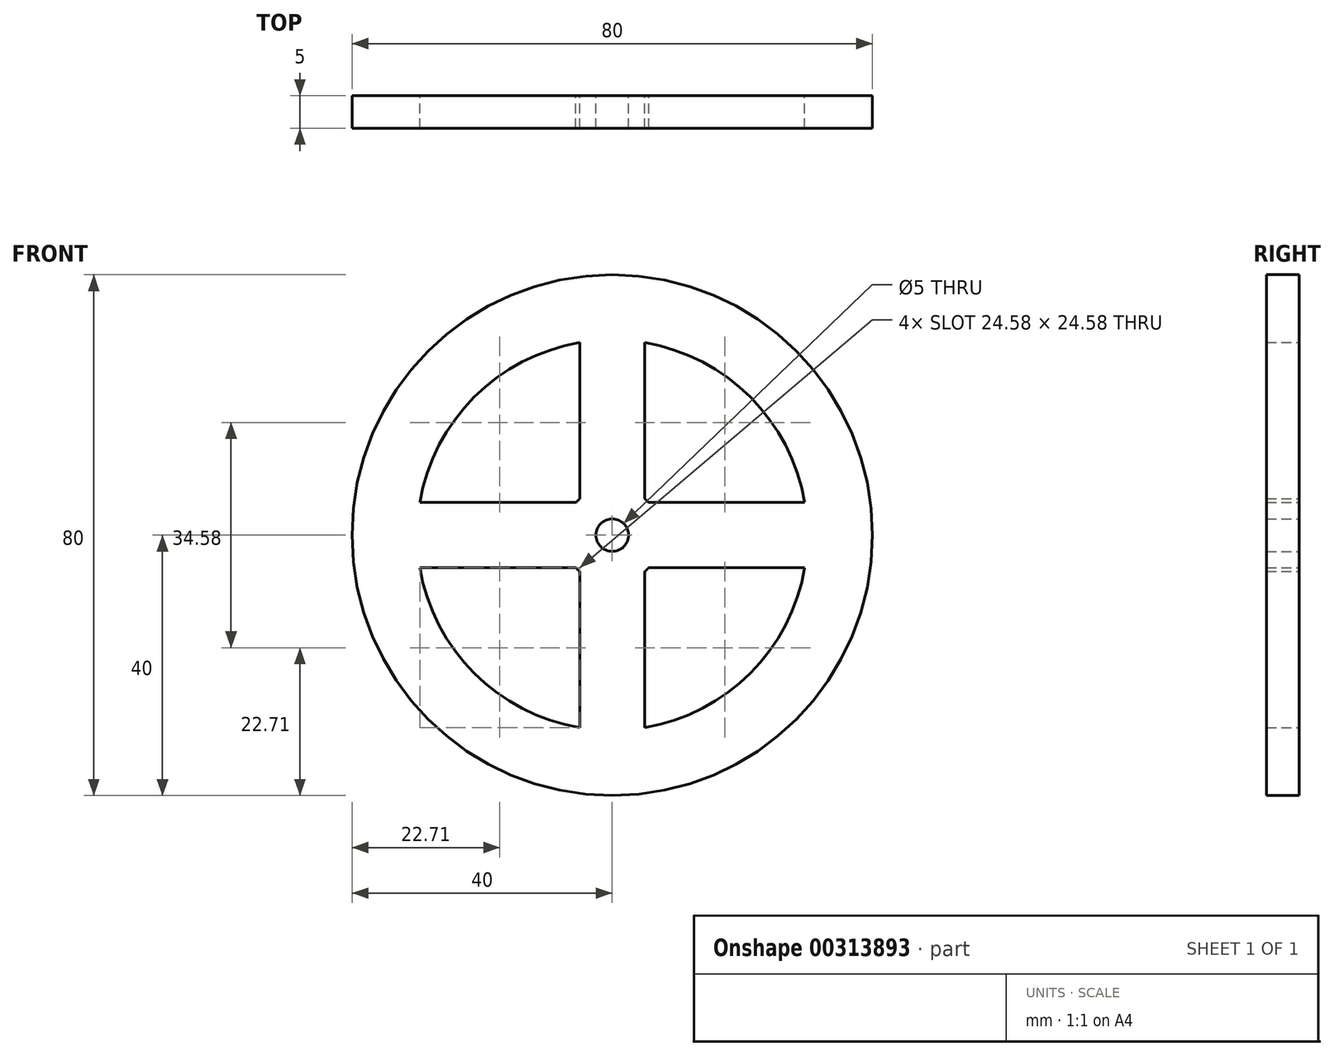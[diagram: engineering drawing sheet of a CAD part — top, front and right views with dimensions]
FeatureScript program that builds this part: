
annotation { "Feature Type Name" : "Feature", "Feature Type Description" : "" }
export const myFeature = defineFeature(function(context is Context, id is Id, definition is map)
    precondition{}
    {
        {
            var Q0;
            Q0=qCreatedBy(makeId("Front.planeOp"),FACE);
            var sketch = newSketch(context, id + "F0", { "sketchPlane" : qUnion([Q0])});
            skCircle(sketch, "E0", {"center": v(0, 0) * mm, "radius": 40 * mm});
            skArc(sketch, "E1", {"start": v(29.58, 5) * mm, "mid": v(21.21, 21.21) * mm, "end": v(5, 29.58) * mm});
            skArc(sketch, "E2", {"start": v(-5.6, -5) * mm, "mid": v(-5.3, -5.3) * mm, "end": v(-5, -5.6) * mm});
            skCircle(sketch, "E3", {"center": v(0, 0) * mm, "radius": 2.5 * mm});
            skLineSegment(sketch, "E4", {"start": v(0, 7.5) * mm, "end": v(0, 30) * mm, "construction": true});
            skLineSegment(sketch, "E5", {"start": v(0, -2.5) * mm, "end": v(0, -30) * mm});
            skLineSegment(sketch, "E6", {"start": v(-7.5, 0) * mm, "end": v(-30, 0) * mm, "construction": true});
            skLineSegment(sketch, "E7", {"start": v(0, 0) * mm, "end": v(0, 2.5) * mm, "construction": true});
            skLineSegment(sketch, "E8", {"start": v(0, 0) * mm, "end": v(2.5, 0) * mm, "construction": true});
            skLineSegment(sketch, "E9", {"start": v(0, 0) * mm, "end": v(0, -30) * mm, "construction": true});
            skLineSegment(sketch, "E10", {"start": v(0, 0) * mm, "end": v(-2.5, 0) * mm, "construction": true});
            skLineSegment(sketch, "E11.0", {"start": v(-5, 5.6) * mm, "end": v(-5, 29.58) * mm});
            skLineSegment(sketch, "E12.0", {"start": v(5, 5.6) * mm, "end": v(5, 29.58) * mm});
            skLineSegment(sketch, "E13.0", {"start": v(5.6, 5) * mm, "end": v(29.58, 5) * mm});
            skLineSegment(sketch, "E14.0", {"start": v(5, -5.6) * mm, "end": v(5, -29.58) * mm});
            skLineSegment(sketch, "E15.0", {"start": v(-5, -5.6) * mm, "end": v(-5, -29.58) * mm});
            skLineSegment(sketch, "E16.0", {"start": v(-5.6, -5) * mm, "end": v(-29.58, -5) * mm});
            skLineSegment(sketch, "E17.0", {"start": v(-5.6, 5) * mm, "end": v(-29.58, 5) * mm});
            skArc(sketch, "E18.trimOffspring", {"start": v(-29.58, -5) * mm, "mid": v(-21.21, -21.21) * mm, "end": v(-5, -29.58) * mm});
            skLineSegment(sketch, "E19.trimOffspring", {"start": v(-7.5, 0) * mm, "end": v(-30, 0) * mm});
            skLineSegment(sketch, "E20.trimOffspring", {"start": v(7.5, 0) * mm, "end": v(30, 0) * mm, "construction": true});
            skLineSegment(sketch, "E21.trimOffspring", {"start": v(0, 7.5) * mm, "end": v(0, 30) * mm});
            skArc(sketch, "E22.trimOffspring", {"start": v(5, -5.6) * mm, "mid": v(5.3, -5.3) * mm, "end": v(5.6, -5) * mm});
            skArc(sketch, "E23.trimOffspring", {"start": v(5.6, 5) * mm, "mid": v(5.3, 5.3) * mm, "end": v(5, 5.6) * mm});
            skArc(sketch, "E24.trimOffspring", {"start": v(-5, 5.6) * mm, "mid": v(-5.3, 5.3) * mm, "end": v(-5.6, 5) * mm});
            skLineSegment(sketch, "E25.0", {"start": v(5.6, -5) * mm, "end": v(29.58, -5) * mm});
            skArc(sketch, "E26.trimOffspring", {"start": v(-5, 29.58) * mm, "mid": v(-21.21, 21.21) * mm, "end": v(-29.58, 5) * mm});
            skArc(sketch, "E27.trimOffspring", {"start": v(5, -29.58) * mm, "mid": v(21.21, -21.21) * mm, "end": v(29.58, -5) * mm});
            skSolve(sketch);
        }
        {
            var Q0;
            Q0 = qSketchRegion(id + "F0", true);
            extrude(context, id + "F1", {"entities" : qUnion([Q0]), "endBound" : BoundingType.SYMMETRIC, "depth" : 5 * mm});
        }
    });
